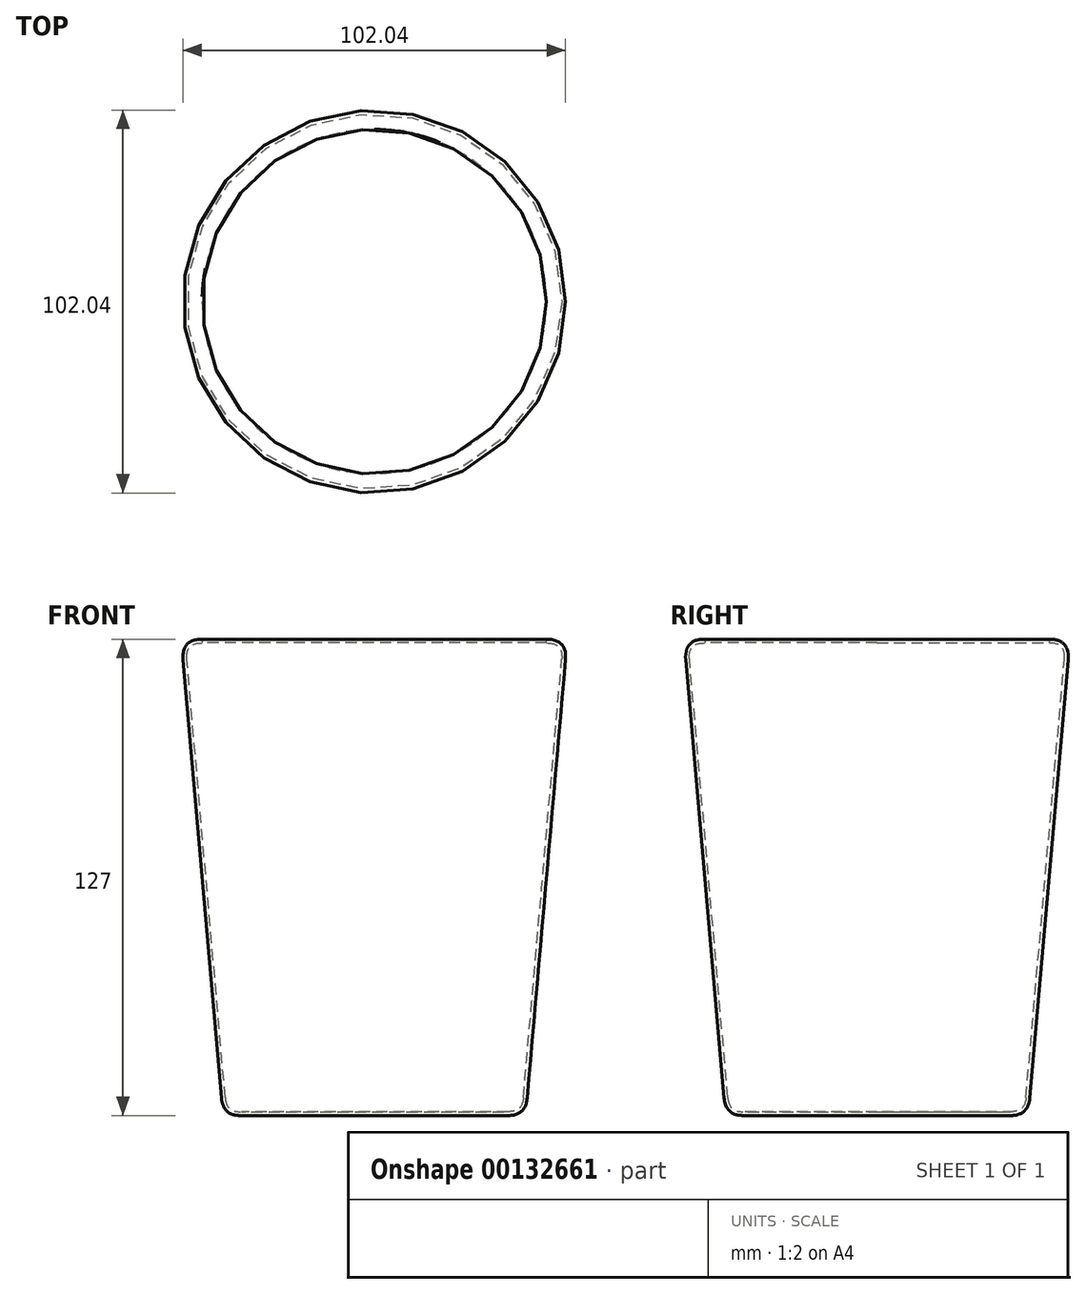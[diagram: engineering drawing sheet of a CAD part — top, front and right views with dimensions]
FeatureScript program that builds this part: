
annotation { "Feature Type Name" : "Feature", "Feature Type Description" : "" }
export const myFeature = defineFeature(function(context is Context, id is Id, definition is map)
    precondition{}
    {
        {
            var Q0;
            Q0=qCreatedBy(makeId("Top.planeOp"),FACE);
            var sketch = newSketch(context, id + "F0", { "sketchPlane" : qUnion([Q0])});
            skCircle(sketch, "E0", {"center": v(0, 0) * mm, "radius": 40.35 * mm});
            skSolve(sketch);
        }
        {
            var Q0;
            Q0=makeQuery(id+"F0.imprint","IMPRINT",FACE,{"disambiguationData":[TD([[makeQuery(id+"F0.imprint","IMPRINT",EDGE,{"derivedFrom":sQuery(id+"F0.wireOp",EDGE,"E0")}),1.0]])]});
            var Q1;
            Q1=sQuery(id+"F0.wireOp",EDGE,"E0");
            extrude(context, id + "F1", {"entities" : qUnion([Q0]), "surfaceEntities" : qUnion([Q1]), "depth" : 127 * mm, "hasDraft" : true, "draftAngle" : 5 * degree});
        }
        {
            var Q0;
            Q0=makeQuery(id+"F1.opExtrude","CAP_FACE",FACE,{"disambiguationData":[OSD([sQuery(id+"F0.wireOp",EDGE,"E0")])],"isStart":false});
            var Q1;
            Q1=makeQuery(id+"F1.opExtrude","CAP_EDGE",EDGE,{"disambiguationData":[OSD([sQuery(id+"F0.wireOp",EDGE,"E0")])],"isStart":true});
            fillet(context, id + "F2", {"entities" : qUnion([Q0, Q1]), "radius" : 5.08 * mm, "rho" : .5, "crossSection" : FilletCrossSection.CONIC, "allowEdgeOverflow" : false});
        }
        {
            var Q0;
            Q0=makeQuery(id+"F1.opExtrude","CAP_FACE",FACE,{"disambiguationData":[OSD([sQuery(id+"F0.wireOp",EDGE,"E0")])],"isStart":false});
            shell(context, id + "F3", {"entities" : qUnion([Q0]), "thickness" : 1 * mm});
        }
    });
